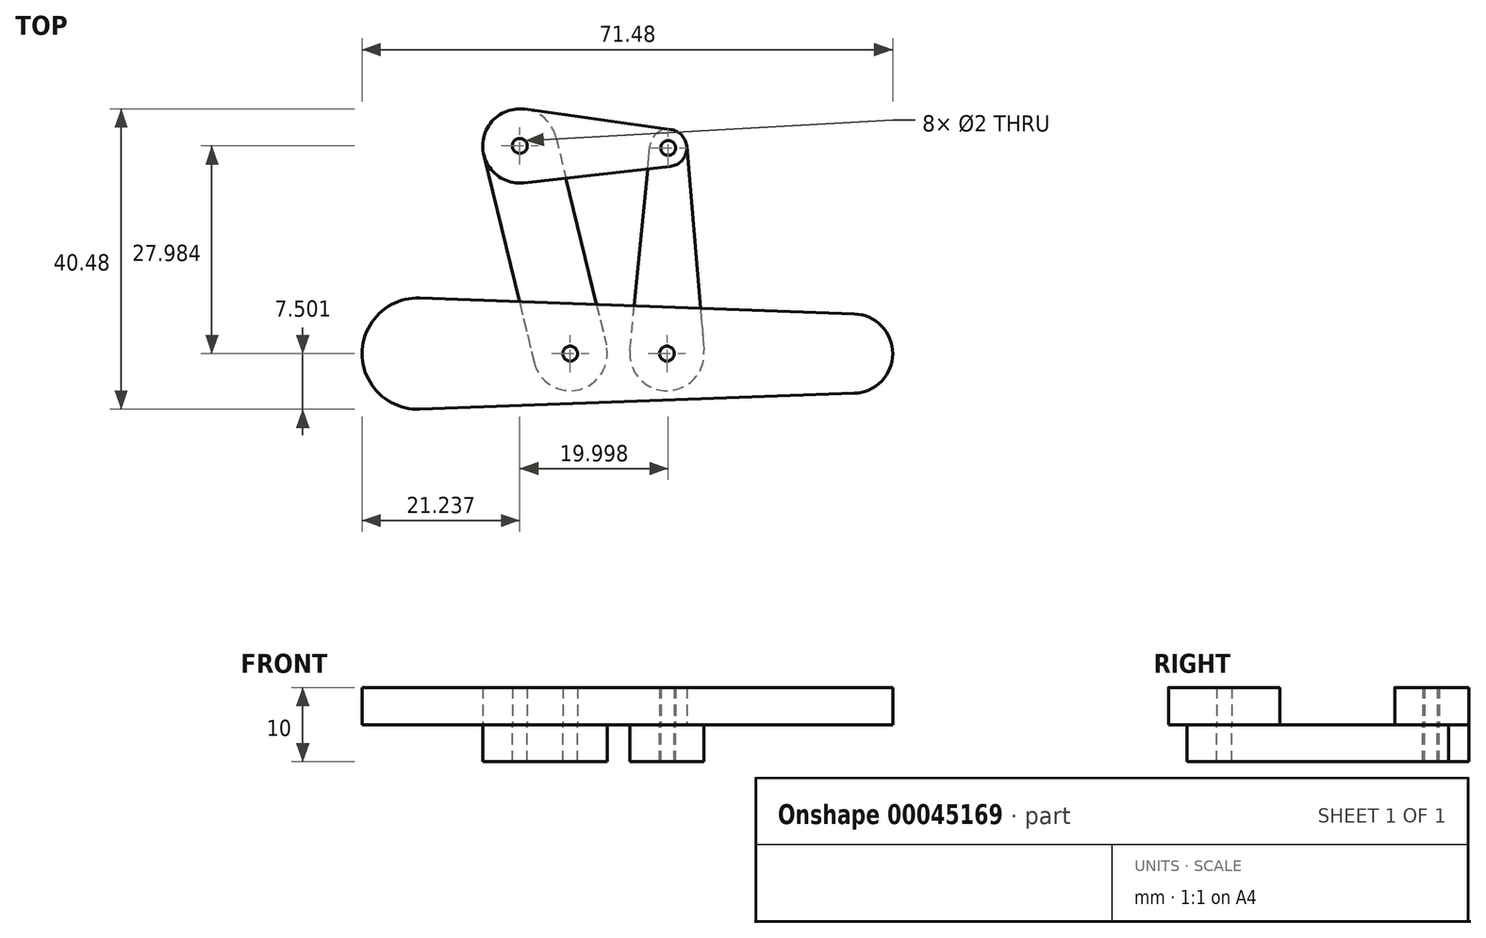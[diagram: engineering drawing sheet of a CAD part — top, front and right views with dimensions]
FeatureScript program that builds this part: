
annotation { "Feature Type Name" : "Feature", "Feature Type Description" : "" }
export const myFeature = defineFeature(function(context is Context, id is Id, definition is map)
    precondition{}
    {
        {
            var Q0;
            Q0=qCreatedBy(makeId("Top.planeOp"),FACE);
            var sketch = newSketch(context, id + "F0", { "sketchPlane" : qUnion([Q0])});
            skLineSegment(sketch, "E0", {"start": v(-16.41, 28) * mm, "end": v(3.58, 27.74) * mm});
            skLineSegment(sketch, "E1", {"start": v(13.52, 17.16) * mm, "end": v(30.38, 6.4) * mm});
            skLineSegment(sketch, "E2", {"start": v(-16.41, 28) * mm, "end": v(13.52, 17.16) * mm, "construction": true});
            skLineSegment(sketch, "E3", {"start": v(3.58, 27.74) * mm, "end": v(30.38, 6.4) * mm, "construction": true});
            skLineSegment(sketch, "E4", {"start": v(-1.45, 22.58) * mm, "end": v(-9.62, 0.02) * mm, "construction": true});
            skLineSegment(sketch, "E5", {"start": v(16.98, 17.07) * mm, "end": v(3.4, 0.02) * mm, "construction": true});
            skLineSegment(sketch, "E6", {"start": v(-49.05, 0.02) * mm, "end": v(41.64, 0.02) * mm, "construction": true});
            skLineSegment(sketch, "E7", {"start": v(-16.41, 28) * mm, "end": v(-9.62, 0.02) * mm, "construction": true});
            skLineSegment(sketch, "E8", {"start": v(13.52, 17.16) * mm, "end": v(-9.62, 0.02) * mm, "construction": true});
            skLineSegment(sketch, "E9", {"start": v(3.58, 27.74) * mm, "end": v(3.4, 0.02) * mm, "construction": true});
            skLineSegment(sketch, "E10", {"start": v(30.38, 6.4) * mm, "end": v(3.4, 0.02) * mm, "construction": true});
            skCircle(sketch, "E11", {"center": v(-16.41, 28) * mm, "radius": 5 * mm});
            skCircle(sketch, "E12", {"center": v(3.58, 27.74) * mm, "radius": 2.5 * mm});
            skLineSegment(sketch, "E13", {"start": v(-15.72, 32.96) * mm, "end": v(3.93, 30.21) * mm});
            skLineSegment(sketch, "E14", {"start": v(-15.85, 23.04) * mm, "end": v(3.86, 25.25) * mm});
            skCircle(sketch, "E15", {"center": v(-9.62, 0.02) * mm, "radius": 5 * mm});
            skCircle(sketch, "E16", {"center": v(3.4, 0.02) * mm, "radius": 5 * mm});
            skLineSegment(sketch, "E17", {"start": v(-21.27, 26.83) * mm, "end": v(-14.48, -1.16) * mm});
            skLineSegment(sketch, "E18", {"start": v(-11.55, 29.18) * mm, "end": v(-4.76, 1.2) * mm});
            skLineSegment(sketch, "E19", {"start": v(-1.57, 0.5) * mm, "end": v(1.1, 27.98) * mm});
            skLineSegment(sketch, "E20", {"start": v(6.08, 27.95) * mm, "end": v(8.39, 0.44) * mm});
            skCircle(sketch, "E21", {"center": v(-30.15, 0.02) * mm, "radius": 7.5 * mm});
            skCircle(sketch, "E22", {"center": v(28.47, 0.02) * mm, "radius": 5.36 * mm});
            skLineSegment(sketch, "E23", {"start": v(-29.88, 7.52) * mm, "end": v(28.67, 5.38) * mm});
            skLineSegment(sketch, "E24", {"start": v(-29.88, -7.47) * mm, "end": v(28.67, -5.33) * mm});
            skCircle(sketch, "E25", {"center": v(-9.62, 0.02) * mm, "radius": 1 * mm});
            skCircle(sketch, "E26", {"center": v(3.4, 0.02) * mm, "radius": 1 * mm});
            skCircle(sketch, "E27", {"center": v(-16.41, 28) * mm, "radius": 1 * mm});
            skCircle(sketch, "E28", {"center": v(3.58, 27.74) * mm, "radius": 1 * mm});
            skSolve(sketch);
        }
        {
            var Q0;
            Q0=makeQuery(id+"F0.imprint","IMPRINT",FACE,{"disambiguationData":[TD([[makeQuery(id+"F0.imprint","IMPRINT",EDGE,{"derivedFrom":sQuery(id+"F0.wireOp",EDGE,"E27")}),-1.0]])]});
            var Q1;
            {var subQ9=sQuery(id+"F0.wireOp",EDGE,"E13");Q1=makeQuery(id+"F0.imprint","IMPRINT",FACE,{"disambiguationData":[TD([[makeQuery(id+"F0.imprint","IMPRINT",EDGE,{"derivedFrom":subQ9}),-1.0]])]});}
            var Q2;
            Q2=makeQuery(id+"F0.imprint","IMPRINT",FACE,{"disambiguationData":[TD([[makeQuery(id+"F0.imprint","IMPRINT",EDGE,{"derivedFrom":sQuery(id+"F0.wireOp",EDGE,"E28")}),-1.0]])]});
            var Q3;
            {var subQ3=sQuery(id+"F0.wireOp",EDGE,"E0");var subQ5=sQuery(id+"F0.wireOp",EDGE,"E12");var subQ7=makeQuery(id+"F0.imprint","INTERSECT",VERTEX,{"derivedFrom":[subQ3,subQ5]});Q3=makeQuery(id+"F0.imprint","IMPRINT",FACE,{"disambiguationData":[TD([[makeQuery(id+"F0.imprint","IMPRINT",EDGE,{"disambiguationData":[TD([[subQ7,1.0]])],"derivedFrom":subQ3}),-1.0]])]});}
            var Q4;
            {var subQ3=sQuery(id+"F0.wireOp",EDGE,"E0");var subQ5=sQuery(id+"F0.wireOp",EDGE,"E18");var subQ7=makeQuery(id+"F0.imprint","INTERSECT",VERTEX,{"derivedFrom":[subQ3,subQ5]});Q4=makeQuery(id+"F0.imprint","IMPRINT",FACE,{"disambiguationData":[TD([[makeQuery(id+"F0.imprint","IMPRINT",EDGE,{"disambiguationData":[TD([[subQ7,-1.0]])],"derivedFrom":subQ3}),-1.0]])]});}
            var Q5;
            {var subQ3=sQuery(id+"F0.wireOp",EDGE,"E0");var subQ5=sQuery(id+"F0.wireOp",EDGE,"E11");var subQ7=makeQuery(id+"F0.imprint","INTERSECT",VERTEX,{"derivedFrom":[subQ3,subQ5]});Q5=makeQuery(id+"F0.imprint","IMPRINT",FACE,{"disambiguationData":[TD([[makeQuery(id+"F0.imprint","IMPRINT",EDGE,{"disambiguationData":[TD([[subQ7,-1.0]])],"derivedFrom":subQ3}),-1.0]])]});}
            var Q6;
            {var subQ0=sQuery(id+"F0.wireOp",EDGE,"E21");var subQ2=makeQuery(id+"F0.imprint","INTERSECT",VERTEX,{"derivedFrom":[subQ0,sQuery(id+"F0.wireOp",EDGE,"E23")]});Q6=makeQuery(id+"F0.imprint","IMPRINT",FACE,{"disambiguationData":[TD([[makeQuery(id+"F0.imprint","IMPRINT",EDGE,{"disambiguationData":[TD([[subQ2,-1.0]])],"derivedFrom":subQ0}),1.0]])]});}
            var Q7;
            {var subQ13=sQuery(id+"F0.wireOp",EDGE,"E24");Q7=makeQuery(id+"F0.imprint","IMPRINT",FACE,{"disambiguationData":[TD([[makeQuery(id+"F0.imprint","IMPRINT",EDGE,{"derivedFrom":subQ13}),1.0]])]});}
            var Q8;
            {var subQ0=sQuery(id+"F0.wireOp",EDGE,"E22");var subQ2=makeQuery(id+"F0.imprint","INTERSECT",VERTEX,{"derivedFrom":[subQ0,sQuery(id+"F0.wireOp",EDGE,"E23")]});Q8=makeQuery(id+"F0.imprint","IMPRINT",FACE,{"disambiguationData":[TD([[makeQuery(id+"F0.imprint","IMPRINT",EDGE,{"disambiguationData":[TD([[subQ2,-1.0]])],"derivedFrom":subQ0}),1.0]])]});}
            var Q9;
            {var subQ1=sQuery(id+"F0.wireOp",EDGE,"E19");var subQ5=sQuery(id+"F0.wireOp",EDGE,"E16");var subQ7=makeQuery(id+"F0.imprint","INTERSECT",VERTEX,{"derivedFrom":[subQ5,subQ1]});Q9=makeQuery(id+"F0.imprint","IMPRINT",FACE,{"disambiguationData":[TD([[makeQuery(id+"F0.imprint","IMPRINT",EDGE,{"disambiguationData":[TD([[subQ7,1.0]])],"derivedFrom":subQ5}),-1.0]])]});}
            var Q10;
            Q10=makeQuery(id+"F0.imprint","IMPRINT",FACE,{"disambiguationData":[TD([[makeQuery(id+"F0.imprint","IMPRINT",EDGE,{"derivedFrom":sQuery(id+"F0.wireOp",EDGE,"E26")}),-1.0]])]});
            var Q11;
            Q11=makeQuery(id+"F0.imprint","IMPRINT",FACE,{"disambiguationData":[TD([[makeQuery(id+"F0.imprint","IMPRINT",EDGE,{"derivedFrom":sQuery(id+"F0.wireOp",EDGE,"E25")}),-1.0]])]});
            var Q12;
            {var subQ3=sQuery(id+"F0.wireOp",EDGE,"E17");var subQ5=sQuery(id+"F0.wireOp",EDGE,"E15");var subQ7=makeQuery(id+"F0.imprint","INTERSECT",VERTEX,{"derivedFrom":[subQ5,subQ3]});Q12=makeQuery(id+"F0.imprint","IMPRINT",FACE,{"disambiguationData":[TD([[makeQuery(id+"F0.imprint","IMPRINT",EDGE,{"disambiguationData":[TD([[subQ7,1.0]])],"derivedFrom":subQ5}),-1.0]])]});}
            var Q13;
            {var subQ1=sQuery(id+"F0.wireOp",EDGE,"E0");var subQ3=sQuery(id+"F0.wireOp",EDGE,"E11");var subQ5=makeQuery(id+"F0.imprint","INTERSECT",VERTEX,{"derivedFrom":[subQ1,subQ3]});Q13=makeQuery(id+"F0.imprint","IMPRINT",FACE,{"disambiguationData":[TD([[makeQuery(id+"F0.imprint","IMPRINT",EDGE,{"disambiguationData":[TD([[subQ5,-1.0]])],"derivedFrom":subQ1}),1.0]])]});}
            var Q14;
            {var subQ1=sQuery(id+"F0.wireOp",EDGE,"E0");var subQ3=sQuery(id+"F0.wireOp",EDGE,"E12");var subQ5=makeQuery(id+"F0.imprint","INTERSECT",VERTEX,{"derivedFrom":[subQ1,subQ3]});Q14=makeQuery(id+"F0.imprint","IMPRINT",FACE,{"disambiguationData":[TD([[makeQuery(id+"F0.imprint","IMPRINT",EDGE,{"disambiguationData":[TD([[subQ5,1.0]])],"derivedFrom":subQ1}),1.0]])]});}
            extrude(context, id + "F1", {"entities" : qUnion([Q0, Q1, Q2, Q3, Q4, Q5, Q6, Q7, Q8, Q9, Q10, Q11, Q12, Q13, Q14]), "depth" : 5 * mm});
        }
        {
            var Q0;
            Q0=makeQuery(id+"F0.imprint","IMPRINT",FACE,{"disambiguationData":[TD([[makeQuery(id+"F0.imprint","IMPRINT",EDGE,{"derivedFrom":sQuery(id+"F0.wireOp",EDGE,"E27")}),-1.0]])]});
            var Q1;
            {var subQ1=sQuery(id+"F0.wireOp",EDGE,"E0");var subQ3=sQuery(id+"F0.wireOp",EDGE,"E11");var subQ5=makeQuery(id+"F0.imprint","INTERSECT",VERTEX,{"derivedFrom":[subQ1,subQ3]});Q1=makeQuery(id+"F0.imprint","IMPRINT",FACE,{"disambiguationData":[TD([[makeQuery(id+"F0.imprint","IMPRINT",EDGE,{"disambiguationData":[TD([[subQ5,-1.0]])],"derivedFrom":subQ1}),1.0]])]});}
            var Q2;
            {var subQ3=sQuery(id+"F0.wireOp",EDGE,"E0");var subQ5=sQuery(id+"F0.wireOp",EDGE,"E11");var subQ7=makeQuery(id+"F0.imprint","INTERSECT",VERTEX,{"derivedFrom":[subQ3,subQ5]});Q2=makeQuery(id+"F0.imprint","IMPRINT",FACE,{"disambiguationData":[TD([[makeQuery(id+"F0.imprint","IMPRINT",EDGE,{"disambiguationData":[TD([[subQ7,-1.0]])],"derivedFrom":subQ3}),-1.0]])]});}
            var Q3;
            {var subQ3=sQuery(id+"F0.wireOp",EDGE,"E14");var subQ7=sQuery(id+"F0.wireOp",EDGE,"E11");var subQ9=makeQuery(id+"F0.imprint","INTERSECT",VERTEX,{"derivedFrom":[subQ7,subQ3]});Q3=makeQuery(id+"F0.imprint","IMPRINT",FACE,{"disambiguationData":[TD([[makeQuery(id+"F0.imprint","IMPRINT",EDGE,{"disambiguationData":[TD([[subQ9,1.0]])],"derivedFrom":subQ7}),-1.0]])]});}
            var Q4;
            {var subQ3=sQuery(id+"F0.wireOp",EDGE,"E17");var subQ5=sQuery(id+"F0.wireOp",EDGE,"E15");var subQ7=makeQuery(id+"F0.imprint","INTERSECT",VERTEX,{"derivedFrom":[subQ5,subQ3]});Q4=makeQuery(id+"F0.imprint","IMPRINT",FACE,{"disambiguationData":[TD([[makeQuery(id+"F0.imprint","IMPRINT",EDGE,{"disambiguationData":[TD([[subQ7,1.0]])],"derivedFrom":subQ5}),-1.0]])]});}
            var Q5;
            Q5=makeQuery(id+"F0.imprint","IMPRINT",FACE,{"disambiguationData":[TD([[makeQuery(id+"F0.imprint","IMPRINT",EDGE,{"derivedFrom":sQuery(id+"F0.wireOp",EDGE,"E25")}),-1.0]])]});
            var Q6;
            Q6=makeQuery(id+"F0.imprint","IMPRINT",FACE,{"disambiguationData":[TD([[makeQuery(id+"F0.imprint","IMPRINT",EDGE,{"derivedFrom":sQuery(id+"F0.wireOp",EDGE,"E26")}),-1.0]])]});
            var Q7;
            {var subQ1=sQuery(id+"F0.wireOp",EDGE,"E19");var subQ5=sQuery(id+"F0.wireOp",EDGE,"E16");var subQ7=makeQuery(id+"F0.imprint","INTERSECT",VERTEX,{"derivedFrom":[subQ5,subQ1]});Q7=makeQuery(id+"F0.imprint","IMPRINT",FACE,{"disambiguationData":[TD([[makeQuery(id+"F0.imprint","IMPRINT",EDGE,{"disambiguationData":[TD([[subQ7,1.0]])],"derivedFrom":subQ5}),-1.0]])]});}
            var Q8;
            {var subQ5=sQuery(id+"F0.wireOp",EDGE,"E12");var subQ7=sQuery(id+"F0.wireOp",EDGE,"E14");var subQ9=makeQuery(id+"F0.imprint","INTERSECT",VERTEX,{"derivedFrom":[subQ5,subQ7]});Q8=makeQuery(id+"F0.imprint","IMPRINT",FACE,{"disambiguationData":[TD([[makeQuery(id+"F0.imprint","IMPRINT",EDGE,{"disambiguationData":[TD([[subQ9,-1.0]])],"derivedFrom":subQ5}),-1.0]])]});}
            var Q9;
            {var subQ3=sQuery(id+"F0.wireOp",EDGE,"E0");var subQ5=sQuery(id+"F0.wireOp",EDGE,"E12");var subQ7=makeQuery(id+"F0.imprint","INTERSECT",VERTEX,{"derivedFrom":[subQ3,subQ5]});Q9=makeQuery(id+"F0.imprint","IMPRINT",FACE,{"disambiguationData":[TD([[makeQuery(id+"F0.imprint","IMPRINT",EDGE,{"disambiguationData":[TD([[subQ7,1.0]])],"derivedFrom":subQ3}),-1.0]])]});}
            var Q10;
            Q10=makeQuery(id+"F0.imprint","IMPRINT",FACE,{"disambiguationData":[TD([[makeQuery(id+"F0.imprint","IMPRINT",EDGE,{"derivedFrom":sQuery(id+"F0.wireOp",EDGE,"E28")}),-1.0]])]});
            var Q11;
            {var subQ1=sQuery(id+"F0.wireOp",EDGE,"E0");var subQ3=sQuery(id+"F0.wireOp",EDGE,"E12");var subQ5=makeQuery(id+"F0.imprint","INTERSECT",VERTEX,{"derivedFrom":[subQ1,subQ3]});Q11=makeQuery(id+"F0.imprint","IMPRINT",FACE,{"disambiguationData":[TD([[makeQuery(id+"F0.imprint","IMPRINT",EDGE,{"disambiguationData":[TD([[subQ5,1.0]])],"derivedFrom":subQ1}),1.0]])]});}
            extrude(context, id + "F2", {"entities" : qUnion([Q0, Q1, Q2, Q3, Q4, Q5, Q6, Q7, Q8, Q9, Q10, Q11]), "oppositeDirection" : true, "depth" : 5 * mm});
        }
    });
